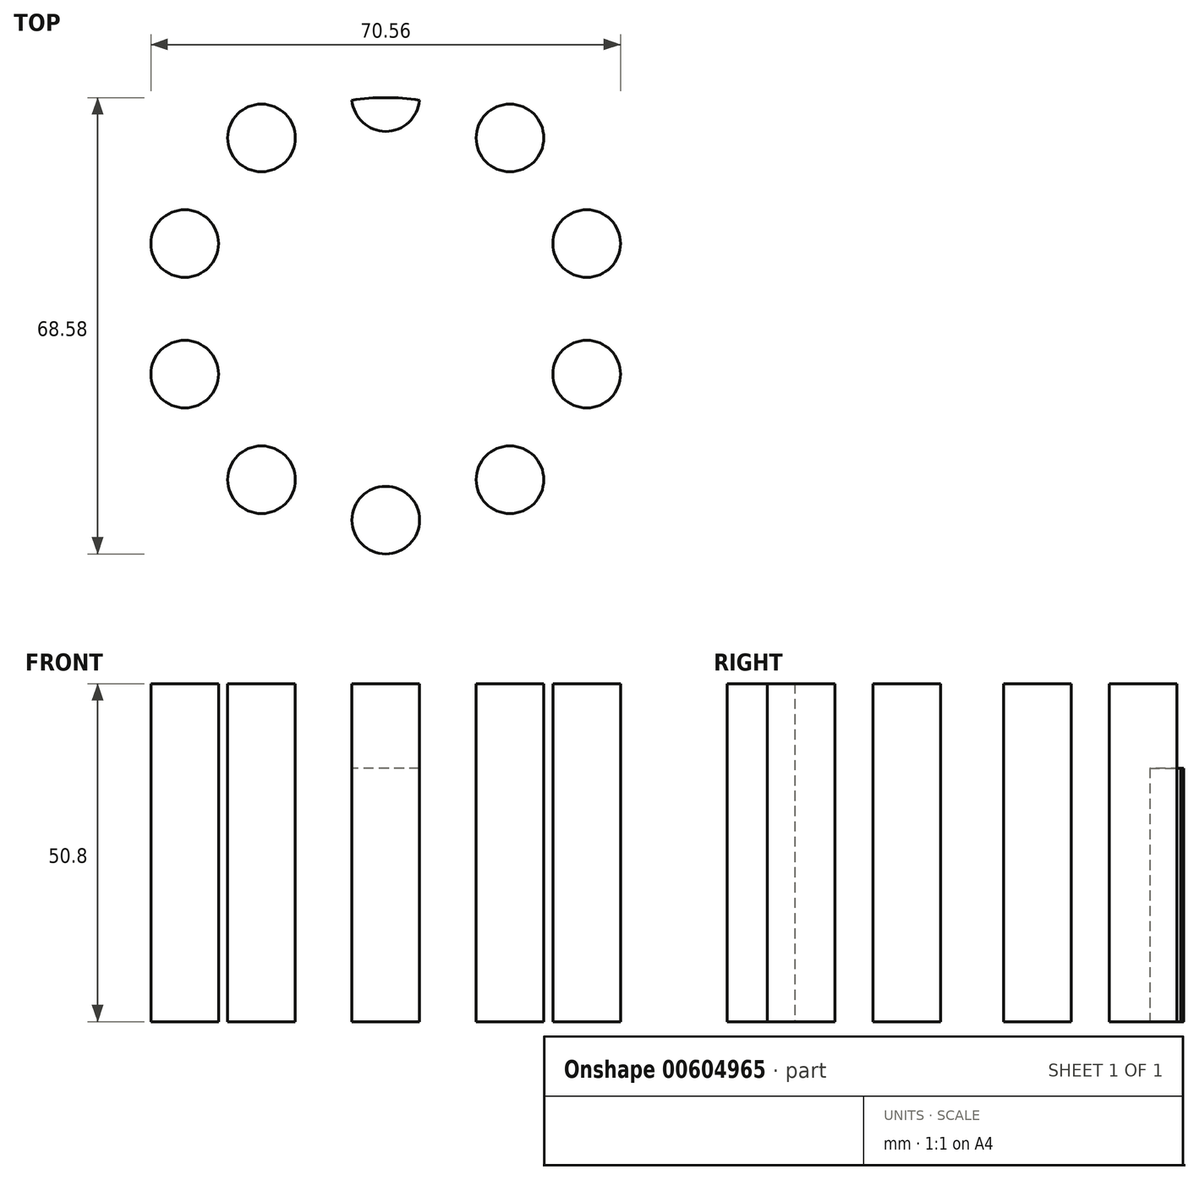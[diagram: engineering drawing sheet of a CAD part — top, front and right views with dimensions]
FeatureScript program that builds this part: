
annotation { "Feature Type Name" : "Feature", "Feature Type Description" : "" }
export const myFeature = defineFeature(function(context is Context, id is Id, definition is map)
    precondition{}
    {
        {
            var Q0;
            Q0=qCreatedBy(makeId("Top.planeOp"),FACE);
            var sketch = newSketch(context, id + "F0", { "sketchPlane" : qUnion([Q0])});
            skCircle(sketch, "E0", {"center": v(0, 0) * mm, "radius": 31.75 * mm});
            skSolve(sketch);
        }
        {
            var Q0;
            Q0=qSketchRegion(id+"F0",true);
            extrude(context, id + "F1", {"entities" : qUnion([Q0]), "depth" : 38.1 * mm});
        }
        {
            var Q0;
            Q0=qCreatedBy(makeId("Top.planeOp"),FACE);
            var sketch = newSketch(context, id + "F2", { "sketchPlane" : qUnion([Q0])});
            skCircle(sketch, "E1", {"center": v(0, 31.75) * mm, "radius": 5.08 * mm});
            skCircle(sketch, "E2.1.0", {"center": v(-18.66, 25.69) * mm, "radius": 5.08 * mm});
            skCircle(sketch, "E2.2.0", {"center": v(-30.2, 9.81) * mm, "radius": 5.08 * mm});
            skCircle(sketch, "E2.3.0", {"center": v(-30.2, -9.81) * mm, "radius": 5.08 * mm});
            skCircle(sketch, "E2.4.0", {"center": v(-18.66, -25.69) * mm, "radius": 5.08 * mm});
            skCircle(sketch, "E2.5.0", {"center": v(0, -31.75) * mm, "radius": 5.08 * mm});
            skCircle(sketch, "E2.6.0", {"center": v(18.66, -25.69) * mm, "radius": 5.08 * mm});
            skCircle(sketch, "E2.7.0", {"center": v(30.2, -9.81) * mm, "radius": 5.08 * mm});
            skCircle(sketch, "E2.8.0", {"center": v(30.2, 9.81) * mm, "radius": 5.08 * mm});
            skCircle(sketch, "E2.9.0", {"center": v(18.66, 25.69) * mm, "radius": 5.08 * mm});
            skPoint(sketch, "E2.center", {"position": v(0, 0) * mm});
            skSolve(sketch);
        }
        {
            var Q0;
            Q0=qSketchRegion(id+"F2",true);
            extrude(context, id + "F3", {"entities" : qUnion([Q0]), "depth" : 50.8 * mm});
        }
        {
            var Q0;
            Q0=makeQuery(id+"F1.opExtrude","SWEPT_BODY",BODY,{"disambiguationData":[OSD([sQuery(id+"F0.wireOp",EDGE,"E0")])]});
            var Q1;
            Q1=makeQuery(id+"F3.opExtrude","SWEPT_BODY",BODY,{"disambiguationData":[OSD([sQuery(id+"F2.wireOp",EDGE,"E1")])]});
            var Q2;
            Q2=makeQuery(id+"F3.opExtrude","SWEPT_BODY",BODY,{"disambiguationData":[OSD([sQuery(id+"F2.wireOp",EDGE,"E2.1.0")])]});
            var Q3;
            Q3=makeQuery(id+"F3.opExtrude","SWEPT_BODY",BODY,{"disambiguationData":[OSD([sQuery(id+"F2.wireOp",EDGE,"E2.2.0")])]});
            var Q4;
            Q4=makeQuery(id+"F3.opExtrude","SWEPT_BODY",BODY,{"disambiguationData":[OSD([sQuery(id+"F2.wireOp",EDGE,"E2.3.0")])]});
            var Q5;
            Q5=makeQuery(id+"F3.opExtrude","SWEPT_BODY",BODY,{"disambiguationData":[OSD([sQuery(id+"F2.wireOp",EDGE,"E2.4.0")])]});
            var Q6;
            Q6=makeQuery(id+"F3.opExtrude","SWEPT_BODY",BODY,{"disambiguationData":[OSD([sQuery(id+"F2.wireOp",EDGE,"E2.5.0")])]});
            var Q7;
            Q7=makeQuery(id+"F3.opExtrude","SWEPT_BODY",BODY,{"disambiguationData":[OSD([sQuery(id+"F2.wireOp",EDGE,"E2.6.0")])]});
            var Q8;
            Q8=makeQuery(id+"F3.opExtrude","SWEPT_BODY",BODY,{"disambiguationData":[OSD([sQuery(id+"F2.wireOp",EDGE,"E2.7.0")])]});
            var Q9;
            Q9=makeQuery(id+"F3.opExtrude","SWEPT_BODY",BODY,{"disambiguationData":[OSD([sQuery(id+"F2.wireOp",EDGE,"E2.8.0")])]});
            var Q10;
            Q10=makeQuery(id+"F3.opExtrude","SWEPT_BODY",BODY,{"disambiguationData":[OSD([sQuery(id+"F2.wireOp",EDGE,"E2.9.0")])]});
            booleanBodies(context, id + "F4", {"operationType" : BooleanOperationType.INTERSECTION, "tools" : qUnion([Q0, Q1, Q2, Q3, Q4, Q5, Q6, Q7, Q8, Q9, Q10]), "keepTools" : true});
        }
        {
            var Q0;
            Q0=makeQuery(id+"F1.opExtrude","SWEPT_BODY",BODY,{"disambiguationData":[OSD([sQuery(id+"F0.wireOp",EDGE,"E0")])]});
            var Q1;
            Q1=makeQuery(id+"F3.opExtrude","SWEPT_BODY",BODY,{"disambiguationData":[OSD([sQuery(id+"F2.wireOp",EDGE,"E1")])]});
            booleanBodies(context, id + "F5", {"operationType" : BooleanOperationType.INTERSECTION, "tools" : qUnion([Q0, Q1])});
        }
    });
